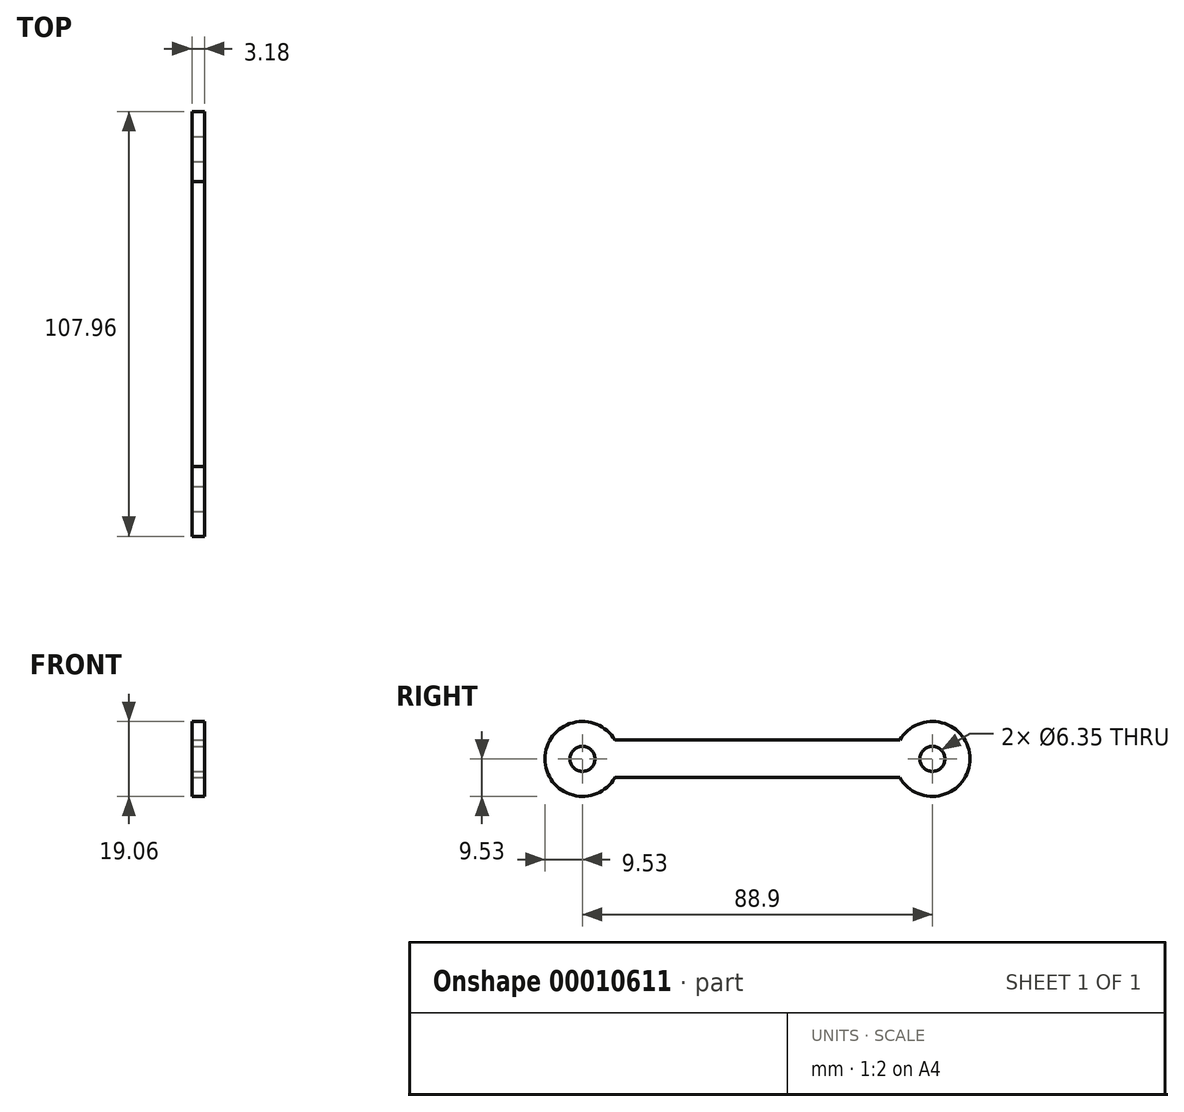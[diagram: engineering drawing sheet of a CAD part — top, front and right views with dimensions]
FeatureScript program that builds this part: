
annotation { "Feature Type Name" : "Feature", "Feature Type Description" : "" }
export const myFeature = defineFeature(function(context is Context, id is Id, definition is map)
    precondition{}
    {
        {
            var Q0;
            Q0=qCreatedBy(makeId("Right.planeOp"),FACE);
            var sketch = newSketch(context, id + "F0", { "sketchPlane" : qUnion([Q0])});
            skCircle(sketch, "E0", {"center": v(0, 0) * mm, "radius": 3.18 * mm});
            skArc(sketch, "E1", {"start": v(8.25, 4.76) * mm, "mid": v(-9.53, 0) * mm, "end": v(8.25, -4.76) * mm});
            skLineSegment(sketch, "E2", {"start": v(-9.52, 0) * mm, "end": v(98.42, 0) * mm, "construction": true});
            skLineSegment(sketch, "E3", {"start": v(44.45, 22.05) * mm, "end": v(44.45, -24.52) * mm, "construction": true});
            skArc(sketch, "E4.0.MirrorC", {"start": v(80.65, 4.76) * mm, "mid": v(98.43, 0) * mm, "end": v(80.65, -4.76) * mm});
            skCircle(sketch, "E5.0.MirrorC", {"center": v(88.9, 0) * mm, "radius": 3.18 * mm});
            skLineSegment(sketch, "E6.rect.bottom", {"start": v(80.65, -4.76) * mm, "end": v(8.25, -4.76) * mm});
            skLineSegment(sketch, "E6.rect.top", {"start": v(80.65, 4.76) * mm, "end": v(8.25, 4.76) * mm});
            skPoint(sketch, "E6.rect.middle", {"position": v(44.45, 0) * mm});
            skSolve(sketch);
        }
        {
            var Q0;
            Q0=qSketchRegion(id+"F0",true);
            extrude(context, id + "F1", {"entities" : qUnion([Q0]), "oppositeDirection" : true, "depth" : 3.17 * mm});
        }
    });
